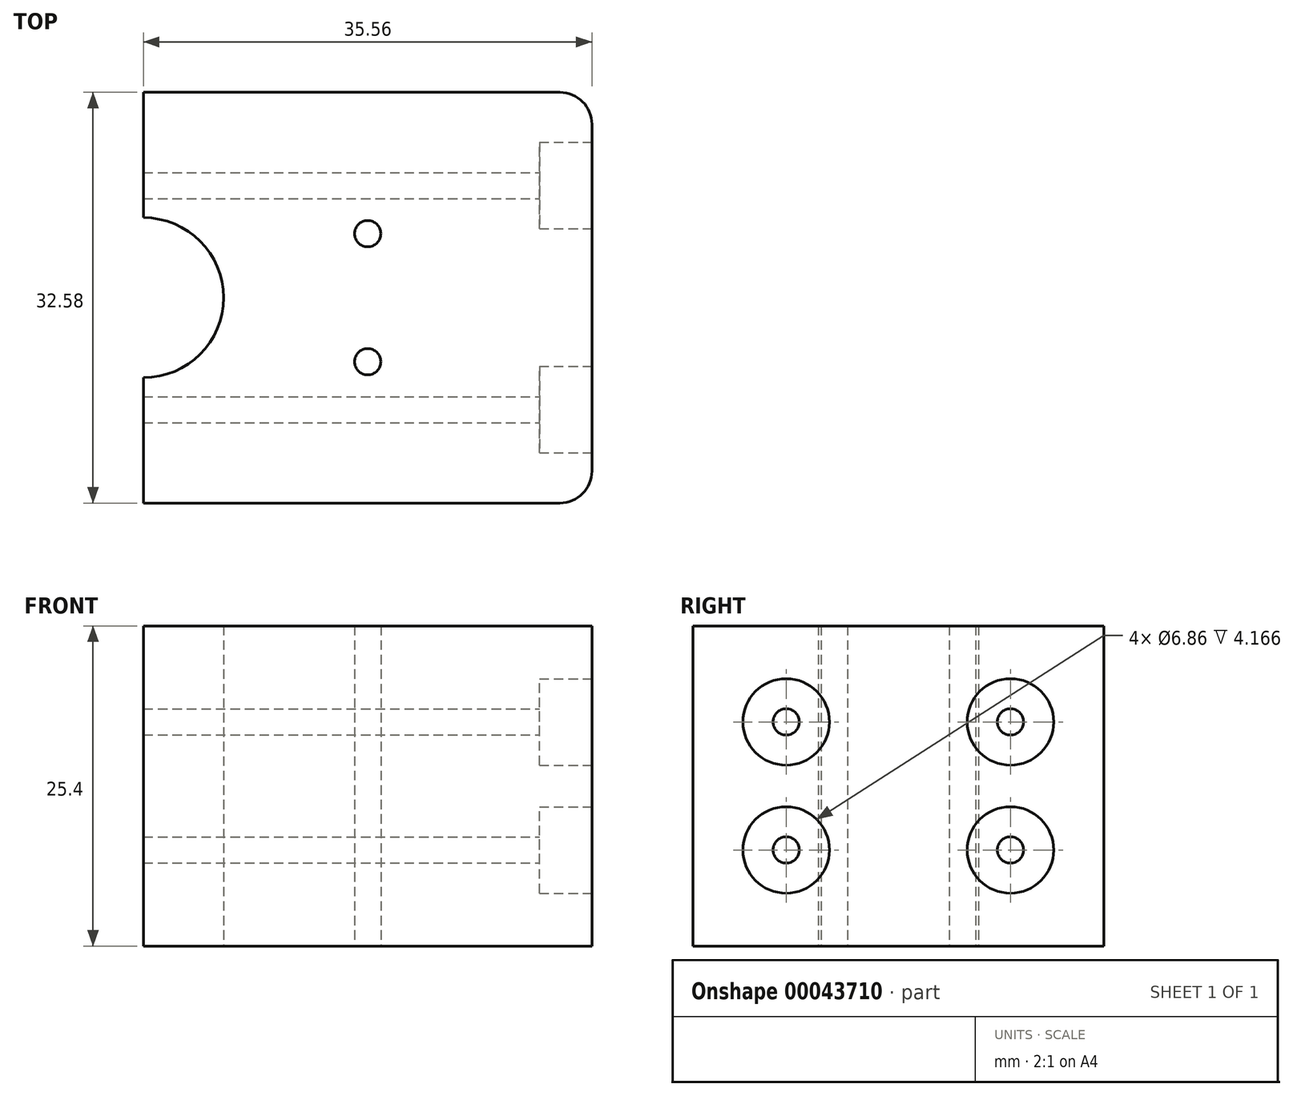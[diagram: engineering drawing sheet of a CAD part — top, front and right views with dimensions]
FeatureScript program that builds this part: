
annotation { "Feature Type Name" : "Feature", "Feature Type Description" : "" }
export const myFeature = defineFeature(function(context is Context, id is Id, definition is map)
    precondition{}
    {
        {
            var Q0;
            Q0=qCreatedBy(makeId("Top.planeOp"),FACE);
            var sketch = newSketch(context, id + "F0", { "sketchPlane" : qUnion([Q0])});
            skLineSegment(sketch, "E0.rect.bottom", {"start": v(-17.78, -16.3) * mm, "end": v(15.24, -16.3) * mm});
            skLineSegment(sketch, "E0.rect.top", {"start": v(-17.78, 16.3) * mm, "end": v(15.24, 16.3) * mm});
            skLineSegment(sketch, "E0.rect.left", {"start": v(-17.78, -16.3) * mm, "end": v(-17.78, -6.35) * mm});
            skLineSegment(sketch, "E0.rect.right", {"start": v(17.78, -13.75) * mm, "end": v(17.78, 13.75) * mm});
            skPoint(sketch, "E0.rect.middle", {"position": v(0, 0) * mm});
            skLineSegment(sketch, "E1", {"start": v(-17.78, 0) * mm, "end": v(17.78, 0) * mm, "construction": true});
            skArc(sketch, "E2", {"start": v(-17.78, -6.35) * mm, "mid": v(-11.43, 0) * mm, "end": v(-17.78, 6.35) * mm});
            skPoint(sketch, "E3.visualSharp", {"position": v(17.78, 16.3) * mm});
            skArc(sketch, "E3.filletArc", {"start": v(17.78, 13.75) * mm, "mid": v(17.04, 15.55) * mm, "end": v(15.24, 16.3) * mm});
            skPoint(sketch, "E4.visualSharp", {"position": v(17.78, -16.3) * mm});
            skArc(sketch, "E4.filletArc", {"start": v(15.24, -16.3) * mm, "mid": v(17.04, -15.55) * mm, "end": v(17.78, -13.75) * mm});
            skLineSegment(sketch, "E5.trimOffspring", {"start": v(-17.78, 6.35) * mm, "end": v(-17.78, 16.3) * mm});
            skLineSegment(sketch, "E6", {"start": v(0, -16.3) * mm, "end": v(0, 16.3) * mm, "construction": true});
            skSolve(sketch);
        }
        {
            var Q0;
            Q0=makeQuery(id+"F0.imprint","IMPRINT",FACE,{"disambiguationData":[TD([[makeQuery(id+"F0.imprint","IMPRINT",EDGE,{"derivedFrom":sQuery(id+"F0.wireOp",EDGE,"E0.rect.bottom")}),1.0]])]});
            extrude(context, id + "F1", {"entities" : qUnion([Q0]), "depth" : 25.4 * mm});
        }
        {
            var Q0;
            Q0=makeQuery(id+"F1.opExtrude","SWEPT_FACE",FACE,{"disambiguationData":[OSD([sQuery(id+"F0.wireOp",EDGE,"E0.rect.right")])]});
            var sketch = newSketch(context, id + "F2", { "sketchPlane" : qUnion([Q0])});
            skLineSegment(sketch, "E7", {"start": v(0, 25.4) * mm, "end": v(0, 0) * mm, "construction": true});
            skLineSegment(sketch, "E8", {"start": v(-13.75, 12.7) * mm, "end": v(13.75, 12.7) * mm, "construction": true});
            skCircle(sketch, "E9", {"center": v(-8.89, 17.78) * mm, "radius": 1.04 * mm});
            skCircle(sketch, "E10.MirrorC", {"center": v(-8.89, 7.62) * mm, "radius": 1.04 * mm});
            skCircle(sketch, "E11.MirrorC", {"center": v(8.9, 17.78) * mm, "radius": 1.04 * mm});
            skCircle(sketch, "E12.MirrorC", {"center": v(8.9, 7.62) * mm, "radius": 1.04 * mm});
            skSolve(sketch);
        }
        {
            var Q0;
            Q0=sQuery(id+"F2.wireOp",VERTEX,"E9.center");
            var Q1;
            Q1=sQuery(id+"F2.wireOp",VERTEX,"E10.MirrorC.center");
            var Q2;
            Q2=sQuery(id+"F2.wireOp",VERTEX,"E11.MirrorC.center");
            var Q3;
            Q3=sQuery(id+"F2.wireOp",VERTEX,"E12.MirrorC.center");
            var Q4;
            Q4=makeQuery(id+"F1.opExtrude","SWEPT_BODY",BODY,{"disambiguationData":[OSD([sQuery(id+"F0.wireOp",EDGE,"E0.rect.bottom"),sQuery(id+"F0.wireOp",EDGE,"E0.rect.top"),sQuery(id+"F0.wireOp",EDGE,"E0.rect.left"),sQuery(id+"F0.wireOp",EDGE,"E0.rect.right"),sQuery(id+"F0.wireOp",EDGE,"E2"),sQuery(id+"F0.wireOp",EDGE,"E3.filletArc"),sQuery(id+"F0.wireOp",EDGE,"E4.filletArc"),sQuery(id+"F0.wireOp",EDGE,"E5.trimOffspring")])]});
            hole(context, id + "F3", {"style" : HoleStyle.C_BORE, "holeDiameter" : 2.08 * mm, "cBoreDiameter" : 6.86 * mm, "cBoreDepth" : 4.17 * mm, "endStyle" : HoleEndStyle.THROUGH, "locations" : qUnion([Q0, Q1, Q2, Q3]), "scope" : qUnion([Q4])});
        }
        {
            var Q0;
            Q0=makeQuery(id+"F1.opExtrude","CAP_FACE",FACE,{"disambiguationData":[OSD([sQuery(id+"F0.wireOp",EDGE,"E0.rect.bottom"),sQuery(id+"F0.wireOp",EDGE,"E0.rect.top"),sQuery(id+"F0.wireOp",EDGE,"E0.rect.left"),sQuery(id+"F0.wireOp",EDGE,"E0.rect.right"),sQuery(id+"F0.wireOp",EDGE,"E2"),sQuery(id+"F0.wireOp",EDGE,"E3.filletArc"),sQuery(id+"F0.wireOp",EDGE,"E4.filletArc"),sQuery(id+"F0.wireOp",EDGE,"E5.trimOffspring")])],"isStart":true});
            var sketch = newSketch(context, id + "F4", { "sketchPlane" : qUnion([Q0])});
            skLineSegment(sketch, "E13", {"start": v(0, 16.3) * mm, "end": v(0, -16.3) * mm, "construction": true});
            skPoint(sketch, "E13.endSnap0", {"position": v(-1.27, -16.3) * mm});
            skLineSegment(sketch, "E14", {"start": v(-11.43, 0) * mm, "end": v(17.78, 0) * mm, "construction": true});
            skCircle(sketch, "E15", {"center": v(0, 5.08) * mm, "radius": 1.04 * mm});
            skCircle(sketch, "E16.MirrorC", {"center": v(0, -5.08) * mm, "radius": 1.04 * mm});
            skSolve(sketch);
        }
        {
            var Q0;
            Q0=sQuery(id+"F4.wireOp",VERTEX,"E15.center");
            var Q1;
            Q1=sQuery(id+"F4.wireOp",VERTEX,"E16.MirrorC.center");
            var Q2;
            Q2=makeQuery(id+"F1.opExtrude","SWEPT_BODY",BODY,{"disambiguationData":[OSD([sQuery(id+"F0.wireOp",EDGE,"E0.rect.bottom"),sQuery(id+"F0.wireOp",EDGE,"E0.rect.top"),sQuery(id+"F0.wireOp",EDGE,"E0.rect.left"),sQuery(id+"F0.wireOp",EDGE,"E0.rect.right"),sQuery(id+"F0.wireOp",EDGE,"E2"),sQuery(id+"F0.wireOp",EDGE,"E3.filletArc"),sQuery(id+"F0.wireOp",EDGE,"E4.filletArc"),sQuery(id+"F0.wireOp",EDGE,"E5.trimOffspring")])]});
            hole(context, id + "F5", {"style" : HoleStyle.SIMPLE, "holeDiameter" : 2.08 * mm, "endStyle" : HoleEndStyle.THROUGH, "locations" : qUnion([Q0, Q1]), "scope" : qUnion([Q2])});
        }
    });
